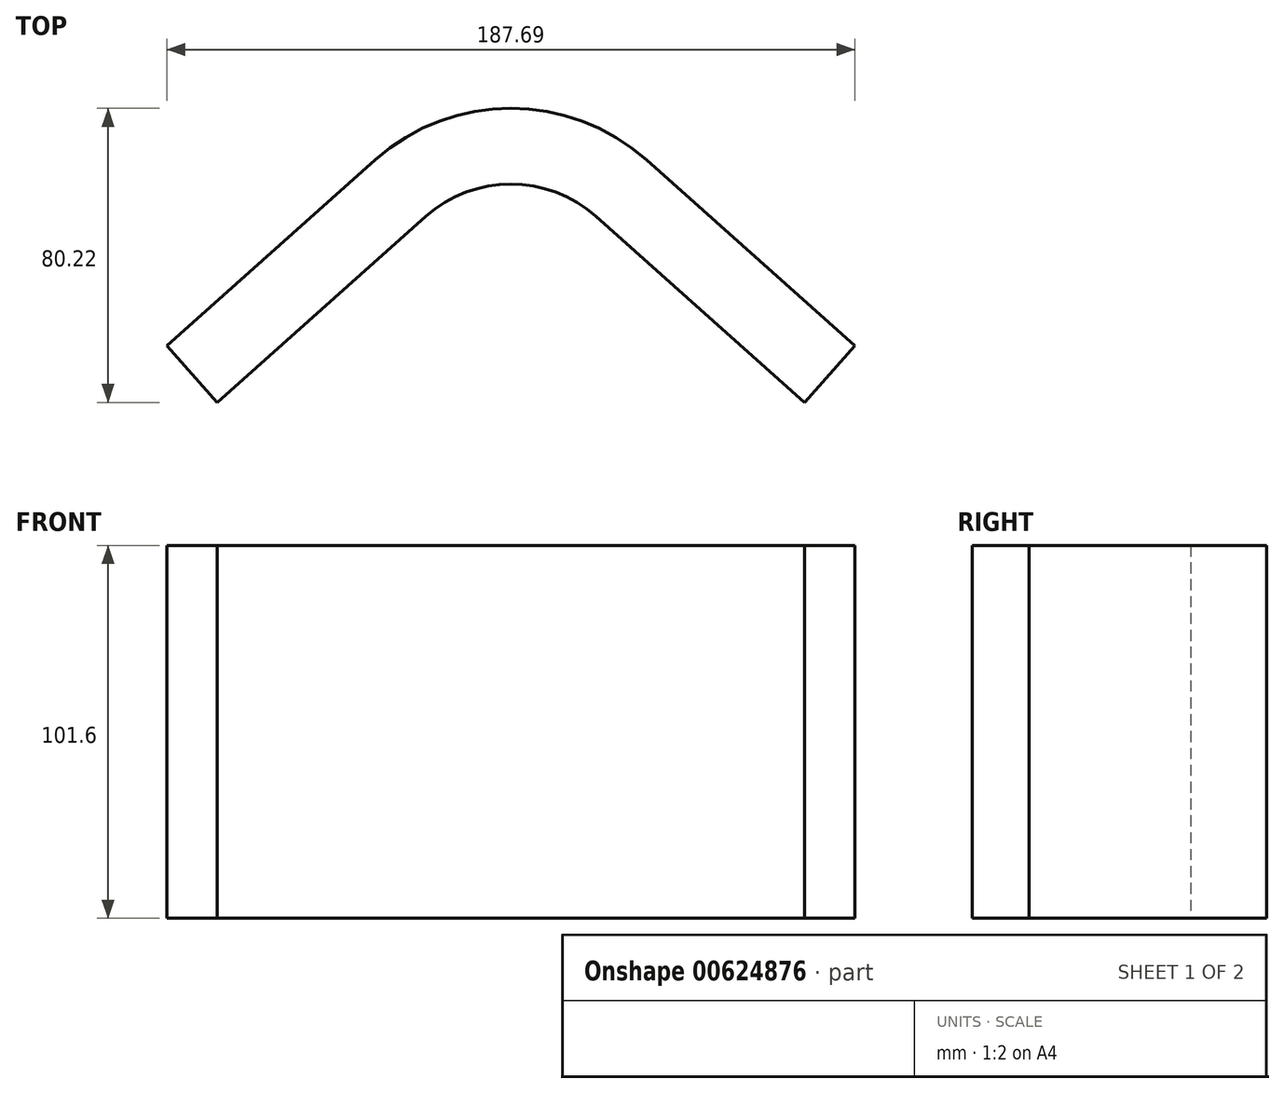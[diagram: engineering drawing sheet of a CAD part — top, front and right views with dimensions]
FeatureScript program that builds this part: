
annotation { "Feature Type Name" : "Feature", "Feature Type Description" : "" }
export const myFeature = defineFeature(function(context is Context, id is Id, definition is map)
    precondition{}
    {
        {
            var Q0;
            Q0=qCreatedBy(makeId("Top.planeOp"),FACE);
            var sketch = newSketch(context, id + "F0", { "sketchPlane" : qUnion([Q0])});
            skLineSegment(sketch, "E0", {"start": v(-46.4, 0) * mm, "end": v(27.54, 0) * mm});
            skArc(sketch, "E1", {"start": v(27.54, 0) * mm, "mid": v(-9.43, 14.09) * mm, "end": v(-46.4, 0) * mm});
            skLineSegment(sketch, "E2", {"start": v(-9.43, 14.09) * mm, "end": v(-9.43, -6.56) * mm, "construction": true});
            skLineSegment(sketch, "E3", {"start": v(-46.4, 0) * mm, "end": v(-103.27, -50.71) * mm});
            skLineSegment(sketch, "E4", {"start": v(-103.27, -50.71) * mm, "end": v(-89.53, -66.13) * mm});
            skLineSegment(sketch, "E5", {"start": v(-89.53, -66.13) * mm, "end": v(-32.65, -15.41) * mm});
            skLineSegment(sketch, "E6", {"start": v(27.54, 0) * mm, "end": v(84.42, -50.71) * mm});
            skLineSegment(sketch, "E7", {"start": v(84.42, -50.71) * mm, "end": v(70.67, -66.13) * mm});
            skLineSegment(sketch, "E8", {"start": v(70.67, -66.13) * mm, "end": v(13.8, -15.41) * mm});
            skArc(sketch, "E9", {"start": v(13.8, -15.41) * mm, "mid": v(-9.43, -6.56) * mm, "end": v(-32.65, -15.41) * mm});
            skSolve(sketch);
        }
        {
            var Q0;
            Q0 = qSketchRegion(id + "F0", true);
            extrude(context, id + "F1", {"entities" : qUnion([Q0]), "depth" : 101.6 * mm, "offsetDistance" : 25.4 * mm});
        }
    });
